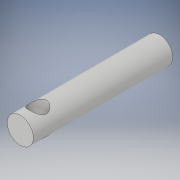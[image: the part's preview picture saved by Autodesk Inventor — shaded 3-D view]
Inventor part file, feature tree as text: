
AUTODESK INVENTOR PART (.ipt)
format: ipt  version: 2019 (Build 230136000, 136)  size: 103,424 bytes
history: native  units: in
note: dims shown in document units (in); Inventor stores cm internally (conversion verified against a paired STEP export)
features: extrude x2, sketch x2, plane x1
ambient origin geometry x8: Origin, YZ Plane, XZ Plane, XY Plane, X Axis, Y Axis, Z Axis, Center Point
bodies: Solid1 (feature_tree)
feature tree (5):
  extrude  "Extrusion1"  Depth=4.0in TaperAngle=0.0deg
  plane  "Work Plane2"
  extrude  "Extrusion3"  Depth=0.5in
  sketch  "Sketch1"  dims[d0=0.75in d1=4.0in d2=0.0in]
  sketch  "Sketch3"  dims[d5=0.5in d6=0.5in d7=1.0in d8=0.0in]
